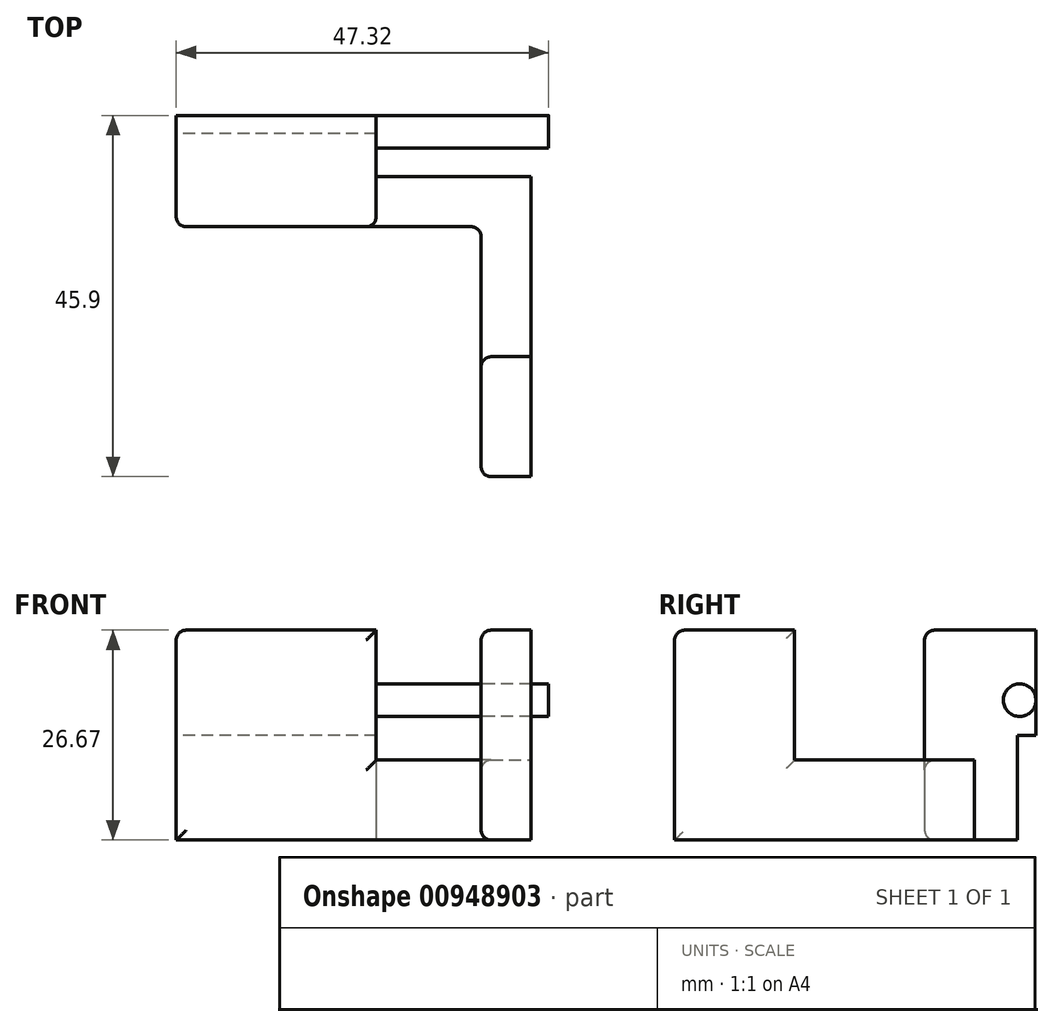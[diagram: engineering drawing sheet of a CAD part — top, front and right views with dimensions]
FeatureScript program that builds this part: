
annotation { "Feature Type Name" : "Feature", "Feature Type Description" : "" }
export const myFeature = defineFeature(function(context is Context, id is Id, definition is map)
    precondition{}
    {
        {
            var Q0;
            Q0=qCreatedBy(makeId("Top.planeOp"),FACE);
            var sketch = newSketch(context, id + "F0", { "sketchPlane" : qUnion([Q0])});
            skLineSegment(sketch, "E0.right", {"start": v(13.33, 1.44) * mm, "end": v(13.33, -3.61) * mm});
            skLineSegment(sketch, "E1.bottom", {"start": v(13.33, 1.44) * mm, "end": v(19.69, 1.44) * mm});
            skLineSegment(sketch, "E1.top", {"start": v(13.34, -36.66) * mm, "end": v(19.69, -36.66) * mm});
            skLineSegment(sketch, "E1.left", {"start": v(13.33, 1.44) * mm, "end": v(13.33, -36.66) * mm});
            skLineSegment(sketch, "E1.right", {"start": v(19.69, 1.44) * mm, "end": v(19.69, -36.66) * mm});
            skLineSegment(sketch, "E2.bottom", {"start": v(13.33, 1.44) * mm, "end": v(0, 1.44) * mm});
            skLineSegment(sketch, "E2.top", {"start": v(13.33, -4.9) * mm, "end": v(0, -4.9) * mm});
            skLineSegment(sketch, "E2.left", {"start": v(13.33, 1.44) * mm, "end": v(13.33, -4.9) * mm});
            skLineSegment(sketch, "E2.right", {"start": v(0, 1.44) * mm, "end": v(0, -4.9) * mm});
            skLineSegment(sketch, "E3.bottom", {"start": v(0, -4.9) * mm, "end": v(-25.4, -4.9) * mm});
            skLineSegment(sketch, "E3.top", {"start": v(0, 6.9) * mm, "end": v(-25.4, 6.9) * mm});
            skLineSegment(sketch, "E3.left", {"start": v(0, -4.9) * mm, "end": v(0, 6.9) * mm});
            skLineSegment(sketch, "E3.right", {"start": v(-25.4, -4.9) * mm, "end": v(-25.4, 6.9) * mm});
            skSolve(sketch);
        }
        {
            var Q0;
            Q0 = qSketchRegion(id + "F0", true);
            extrude(context, id + "F1", {"entities" : qUnion([Q0]), "depth" : 26.67 * mm, "offsetDistance" : 25.4 * mm});
        }
        {
            var Q0;
            Q0=makeQuery(id+"F1.opExtrude","CAP_FACE",FACE,{"disambiguationData":[OSD([sQuery(id+"F0.wireOp",EDGE,"E1.bottom"),sQuery(id+"F0.wireOp",EDGE,"E1.top"),sQuery(id+"F0.wireOp",EDGE,"E1.left"),sQuery(id+"F0.wireOp",EDGE,"E1.right"),sQuery(id+"F0.wireOp",EDGE,"E2.bottom"),sQuery(id+"F0.wireOp",EDGE,"E2.top"),sQuery(id+"F0.wireOp",EDGE,"E3.bottom"),sQuery(id+"F0.wireOp",EDGE,"E3.top"),sQuery(id+"F0.wireOp",EDGE,"E3.left"),sQuery(id+"F0.wireOp",EDGE,"E3.right")])],"isStart":false});
            var sketch = newSketch(context, id + "F2", { "sketchPlane" : qUnion([Q0])});
            skLineSegment(sketch, "E4.bottom", {"start": v(0, 1.44) * mm, "end": v(13.33, 1.44) * mm});
            skLineSegment(sketch, "E4.top", {"start": v(0, -4.9) * mm, "end": v(13.33, -4.9) * mm});
            skLineSegment(sketch, "E4.left", {"start": v(0, 1.44) * mm, "end": v(0, -4.9) * mm});
            skLineSegment(sketch, "E4.right", {"start": v(13.33, 1.44) * mm, "end": v(13.33, -4.9) * mm});
            skLineSegment(sketch, "E5.bottom", {"start": v(13.33, 1.44) * mm, "end": v(19.69, 1.44) * mm});
            skLineSegment(sketch, "E5.top", {"start": v(13.33, -21.42) * mm, "end": v(19.69, -21.42) * mm});
            skLineSegment(sketch, "E5.left", {"start": v(13.33, 1.44) * mm, "end": v(13.33, -21.42) * mm});
            skLineSegment(sketch, "E5.right", {"start": v(19.69, 1.44) * mm, "end": v(19.69, -21.42) * mm});
            skSolve(sketch);
        }
        {
            var Q0;
            Q0 = qSketchRegion(id + "F2", true);
            extrude(context, id + "F3", {"entities" : qUnion([Q0]), "operationType" : NewBodyOperationType.REMOVE, "oppositeDirection" : true, "depth" : 16.5 * mm, "offsetDistance" : 25.4 * mm});
        }
        {
            var Q0;
            Q0=makeQuery(id+"F1.opExtrude","SWEPT_FACE",FACE,{"disambiguationData":[OSD([sQuery(id+"F0.wireOp",EDGE,"E3.top")])]});
            var sketch = newSketch(context, id + "F4", { "sketchPlane" : qUnion([Q0])});
            skLineSegment(sketch, "E6.bottom", {"start": v(0, 26.67) * mm, "end": v(25.4, 26.67) * mm});
            skLineSegment(sketch, "E6.top", {"start": v(0, 13.33) * mm, "end": v(25.4, 13.33) * mm});
            skLineSegment(sketch, "E6.left", {"start": v(0, 26.67) * mm, "end": v(0, 13.33) * mm});
            skLineSegment(sketch, "E6.right", {"start": v(25.4, 26.67) * mm, "end": v(25.4, 13.33) * mm});
            skSolve(sketch);
        }
        {
            var Q0;
            Q0 = qSketchRegion(id + "F4", true);
            extrude(context, id + "F5", {"entities" : qUnion([Q0]), "operationType" : NewBodyOperationType.ADD, "depth" : 2.32 * mm, "offsetDistance" : 25.4 * mm});
        }
        {
            var Q0;
            Q0=makeQuery(id+"F3.boolean.opBoolean","MERGE",FACE,{"derivedFrom":[makeQuery(id+"F1.opExtrude","SWEPT_FACE",FACE,{"disambiguationData":[OSD([sQuery(id+"F0.wireOp",EDGE,"E3.left")])]})],"fromTools":[makeQuery(id+"F3.opExtrude","SWEPT_FACE",FACE,{"disambiguationData":[OSD([sQuery(id+"F2.wireOp",EDGE,"E4.left")])]})]});
            var sketch = newSketch(context, id + "F6", { "sketchPlane" : qUnion([Q0])});
            skLineSegment(sketch, "E7", {"start": v(7.17, 26.67) * mm, "end": v(7.17, 0) * mm, "construction": true});
            skCircle(sketch, "E8", {"center": v(7.17, 17.78) * mm, "radius": 2.07 * mm});
            skSolve(sketch);
        }
        {
            var Q0;
            Q0 = qSketchRegion(id + "F6", true);
            var Q1;
            Q1=makeQuery(id+"F1.opExtrude","SWEPT_FACE",FACE,{"disambiguationData":[OSD([sQuery(id+"F0.wireOp",EDGE,"E1.right")])]});
            extrude(context, id + "F7", {"entities" : qUnion([Q0]), "operationType" : NewBodyOperationType.ADD, "endBound" : BoundingType.UP_TO_SURFACE, "depth" : 25.4 * mm, "endBoundEntityFace" : qUnion([Q1]), "hasOffset" : true, "offsetDistance" : 2.24 * mm, "offsetOppositeDirection" : true});
        }
        {
            var Q0;
            Q0=makeQuery(id+"F1.opExtrude","SWEPT_FACE",FACE,{"disambiguationData":[OSD([sQuery(id+"F0.wireOp",EDGE,"E2.top"),sQuery(id+"F0.wireOp",EDGE,"E3.bottom")])]});
            var Q1;
            Q1=makeQuery(id+"F1.opExtrude","SWEPT_FACE",FACE,{"disambiguationData":[OSD([sQuery(id+"F0.wireOp",EDGE,"E1.left")])]});
            var Q2;
            Q2=makeQuery(id+"F1.opExtrude","CAP_EDGE",EDGE,{"disambiguationData":[OSD([sQuery(id+"F0.wireOp",EDGE,"E3.right")])],"isStart":false});
            var Q3;
            Q3=makeQuery(id+"F1.opExtrude","CAP_EDGE",EDGE,{"disambiguationData":[OSD([sQuery(id+"F0.wireOp",EDGE,"E1.top")])],"isStart":false});
            var Q4;
            Q4=makeQuery(id+"F1.opExtrude","CAP_EDGE",EDGE,{"disambiguationData":[OSD([sQuery(id+"F0.wireOp",EDGE,"E1.left")])],"isStart":true});
            fillet(context, id + "F8", {"entities" : qUnion([Q0, Q1, Q2, Q3, Q4]), "tangentPropagation" : true, "radius" : 1.27 * mm, "defaultsChanged" : false, "vertexSettings" : [], "allowEdgeOverflow" : false});
        }
    });
